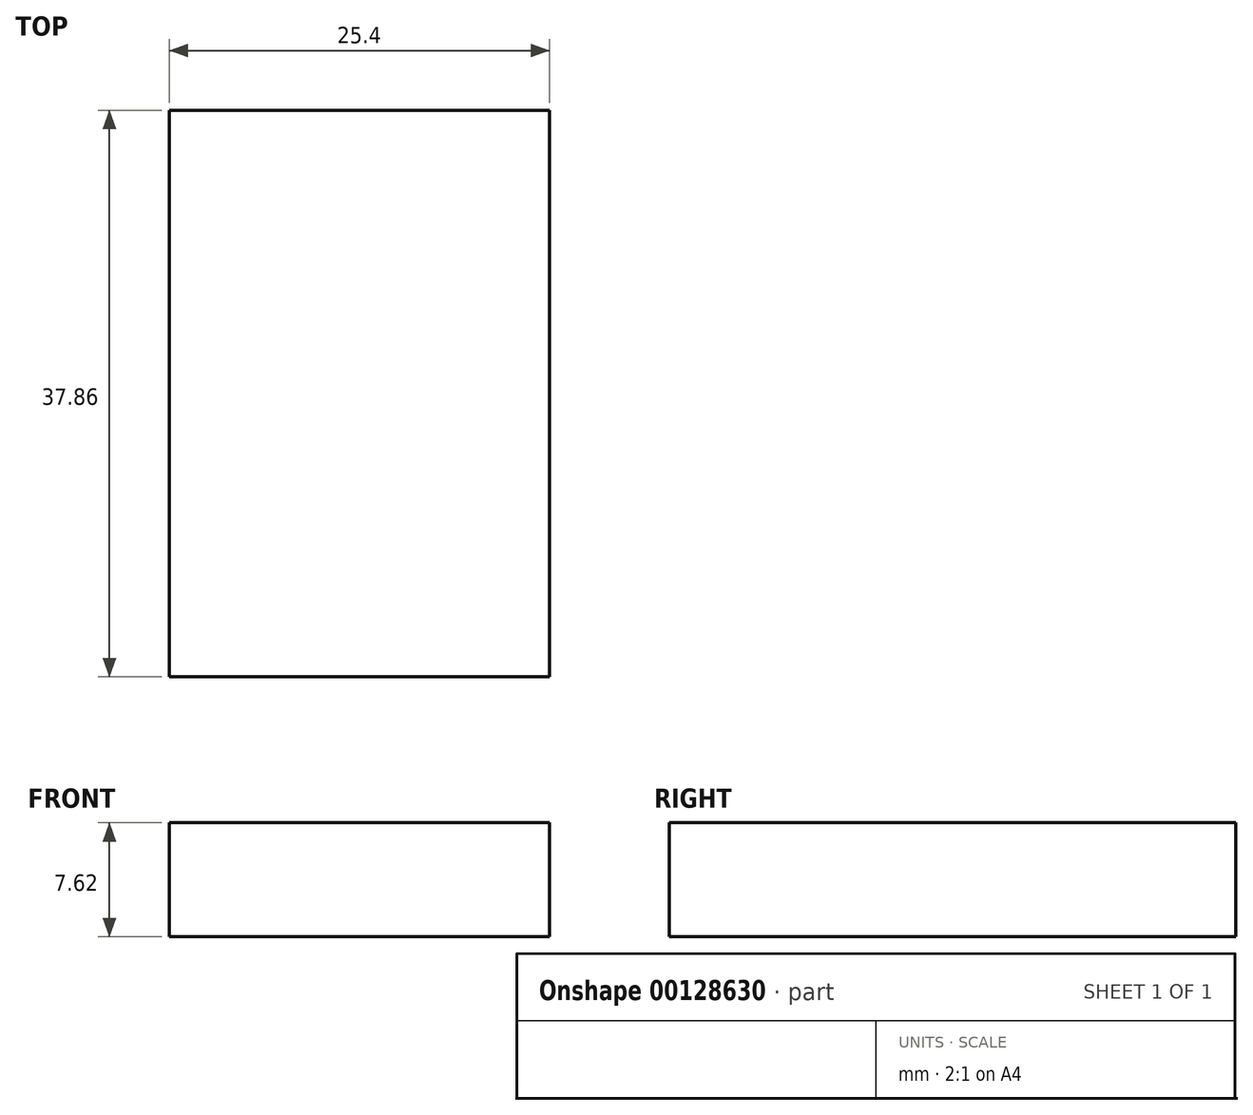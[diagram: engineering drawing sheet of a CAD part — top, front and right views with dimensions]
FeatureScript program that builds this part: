
annotation { "Feature Type Name" : "Feature", "Feature Type Description" : "" }
export const myFeature = defineFeature(function(context is Context, id is Id, definition is map)
    precondition{}
    {
        {
            var Q0;
            Q0=qCreatedBy(makeId("Top.planeOp"),FACE);
            var sketch = newSketch(context, id + "F0", { "sketchPlane" : qUnion([Q0])});
            skLineSegment(sketch, "E0.bottom", {"start": v(-24.7, 20.49) * mm, "end": v(0.7, 20.49) * mm});
            skLineSegment(sketch, "E0.top", {"start": v(-24.7, -17.37) * mm, "end": v(0.7, -17.37) * mm});
            skLineSegment(sketch, "E0.left", {"start": v(-24.7, 20.49) * mm, "end": v(-24.7, -17.37) * mm});
            skLineSegment(sketch, "E0.right", {"start": v(0.7, 20.49) * mm, "end": v(0.7, -17.37) * mm});
            skSolve(sketch);
        }
        {
            var Q0;
            Q0=makeQuery(id+"F0.imprint","IMPRINT",FACE,{"disambiguationData":[TD([[makeQuery(id+"F0.imprint","IMPRINT",EDGE,{"derivedFrom":sQuery(id+"F0.wireOp",EDGE,"E0.bottom")}),-1.0]])]});
            extrude(context, id + "F1", {"entities" : qUnion([Q0]), "depth" : 7.62 * mm});
        }
    });
